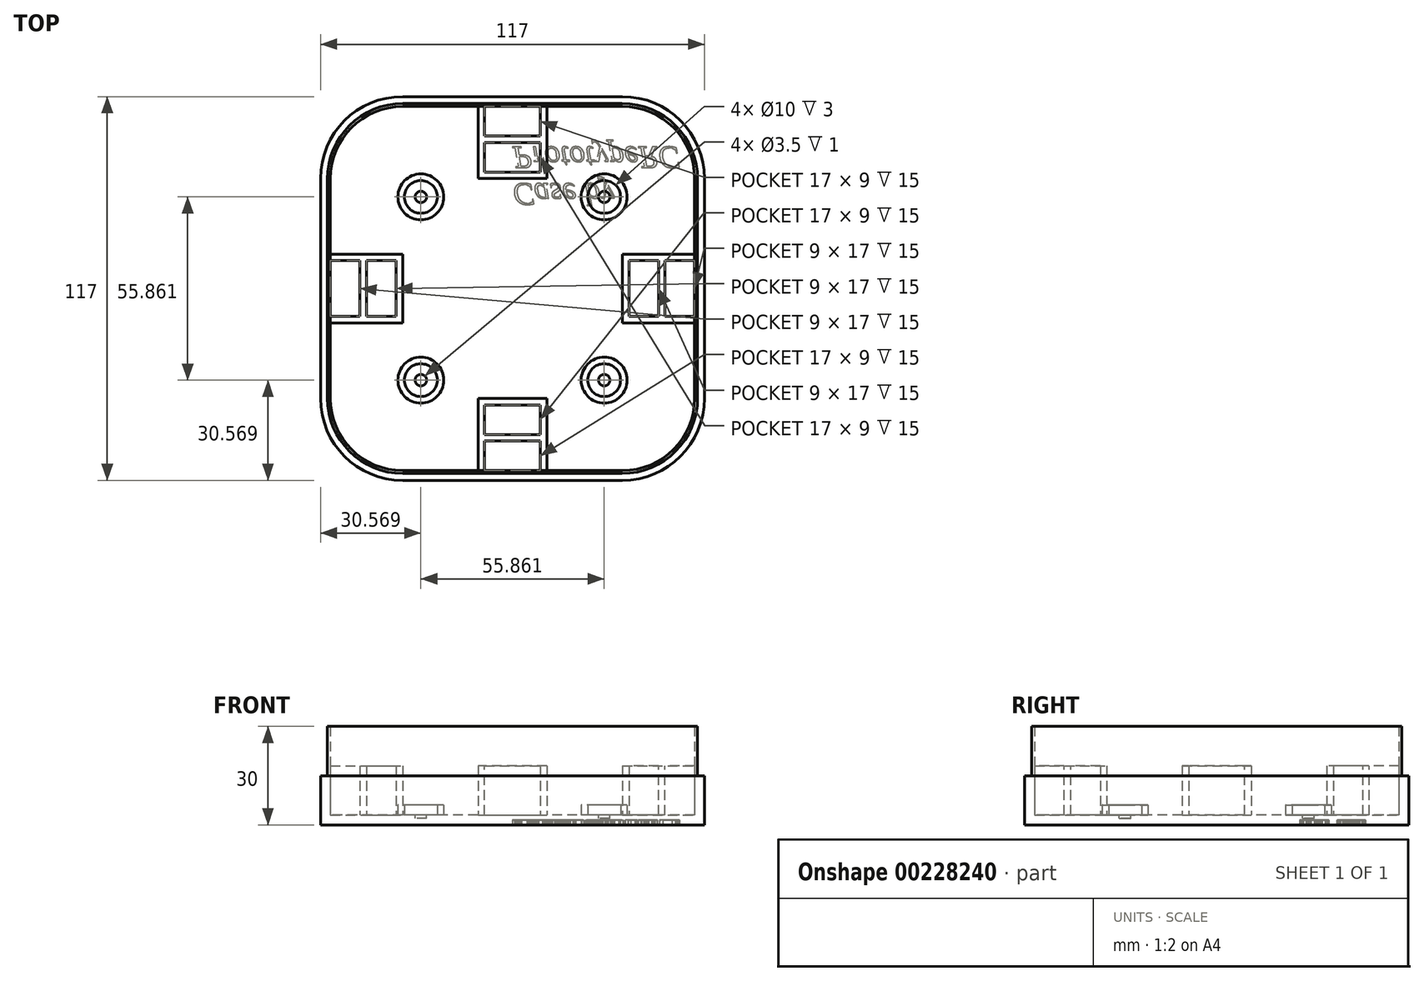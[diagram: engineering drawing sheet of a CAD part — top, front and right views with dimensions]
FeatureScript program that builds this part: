
annotation { "Feature Type Name" : "Feature", "Feature Type Description" : "" }
export const myFeature = defineFeature(function(context is Context, id is Id, definition is map)
    precondition{}
    {
        {
            var Q0;
            Q0=qCreatedBy(makeId("Top.planeOp"),FACE);
            var sketch = newSketch(context, id + "F0", { "sketchPlane" : qUnion([Q0])});
            skLineSegment(sketch, "E0.bottom", {"start": v(33.5, 58.5) * mm, "end": v(-33.5, 58.5) * mm});
            skLineSegment(sketch, "E0.top", {"start": v(33.5, -58.5) * mm, "end": v(-33.5, -58.5) * mm});
            skLineSegment(sketch, "E0.left", {"start": v(58.5, 33.5) * mm, "end": v(58.5, -33.5) * mm});
            skLineSegment(sketch, "E0.right", {"start": v(-58.5, 33.5) * mm, "end": v(-58.5, -33.5) * mm});
            skPoint(sketch, "E0.middle", {"position": v(0, 0) * mm});
            skPoint(sketch, "E1.visualSharp", {"position": v(-58.5, -58.5) * mm});
            skArc(sketch, "E1.filletArc", {"start": v(-58.5, -33.5) * mm, "mid": v(-51.18, -51.18) * mm, "end": v(-33.5, -58.5) * mm});
            skPoint(sketch, "E2.visualSharp", {"position": v(58.5, -58.5) * mm});
            skArc(sketch, "E2.filletArc", {"start": v(33.5, -58.5) * mm, "mid": v(51.18, -51.18) * mm, "end": v(58.5, -33.5) * mm});
            skPoint(sketch, "E3.visualSharp", {"position": v(58.5, 58.5) * mm});
            skArc(sketch, "E3.filletArc", {"start": v(58.5, 33.5) * mm, "mid": v(51.18, 51.18) * mm, "end": v(33.5, 58.5) * mm});
            skPoint(sketch, "E4.visualSharp", {"position": v(-58.5, 58.5) * mm});
            skArc(sketch, "E4.filletArc", {"start": v(-33.5, 58.5) * mm, "mid": v(-51.18, 51.18) * mm, "end": v(-58.5, 33.5) * mm});
            skSolve(sketch);
        }
        {
            var Q0;
            Q0 = qSketchRegion(id + "F0", true);
            extrude(context, id + "F1", {"entities" : qUnion([Q0]), "depth" : 30 * mm});
        }
        {
            var Q0;
            Q0=makeQuery(id+"F1.opExtrude","CAP_FACE",FACE,{"disambiguationData":[OSD([sQuery(id+"F0.wireOp",EDGE,"E0.bottom"),sQuery(id+"F0.wireOp",EDGE,"E0.top"),sQuery(id+"F0.wireOp",EDGE,"E0.left"),sQuery(id+"F0.wireOp",EDGE,"E0.right")])],"isStart":false});
            shell(context, id + "F2", {"entities" : qUnion([Q0]), "thickness" : 3 * mm});
        }
        {
            var Q0;
            Q0=makeQuery(id+"F1.opExtrude","CAP_FACE",FACE,{"disambiguationData":[OSD([sQuery(id+"F0.wireOp",EDGE,"E0.bottom"),sQuery(id+"F0.wireOp",EDGE,"E0.top"),sQuery(id+"F0.wireOp",EDGE,"E0.left"),sQuery(id+"F0.wireOp",EDGE,"E0.right")])],"isStart":false});
            var sketch = newSketch(context, id + "F3", { "sketchPlane" : qUnion([Q0])});
            skPoint(sketch, "E5.middle", {"position": v(0, 0) * mm});
            skLineSegment(sketch, "E6.bottom", {"start": v(33.4, 56.4) * mm, "end": v(-33.4, 56.4) * mm});
            skLineSegment(sketch, "E6.top", {"start": v(33.4, -56.4) * mm, "end": v(-33.4, -56.4) * mm});
            skLineSegment(sketch, "E6.left", {"start": v(56.4, 33.4) * mm, "end": v(56.4, -33.4) * mm});
            skLineSegment(sketch, "E6.right", {"start": v(-56.4, 33.4) * mm, "end": v(-56.4, -33.4) * mm});
            skPoint(sketch, "E7.visualSharp", {"position": v(56.4, 56.4) * mm});
            skArc(sketch, "E7.filletArc", {"start": v(56.4, 33.4) * mm, "mid": v(49.66, 49.66) * mm, "end": v(33.4, 56.4) * mm});
            skPoint(sketch, "E8.visualSharp", {"position": v(56.4, -56.4) * mm});
            skArc(sketch, "E8.filletArc", {"start": v(33.4, -56.4) * mm, "mid": v(49.66, -49.66) * mm, "end": v(56.4, -33.4) * mm});
            skPoint(sketch, "E9.visualSharp", {"position": v(-56.4, -56.4) * mm});
            skArc(sketch, "E9.filletArc", {"start": v(-56.4, -33.4) * mm, "mid": v(-49.66, -49.66) * mm, "end": v(-33.4, -56.4) * mm});
            skPoint(sketch, "E10.visualSharp", {"position": v(-56.4, 56.4) * mm});
            skArc(sketch, "E10.filletArc", {"start": v(-33.4, 56.4) * mm, "mid": v(-49.66, 49.66) * mm, "end": v(-56.4, 33.4) * mm});
            skLineSegment(sketch, "E11.bottom", {"start": v(33.5, 58.5) * mm, "end": v(-33.5, 58.5) * mm});
            skLineSegment(sketch, "E11.top", {"start": v(33.5, -58.5) * mm, "end": v(-33.5, -58.5) * mm});
            skLineSegment(sketch, "E11.left", {"start": v(58.5, 33.5) * mm, "end": v(58.5, -33.5) * mm});
            skLineSegment(sketch, "E11.right", {"start": v(-58.5, 33.5) * mm, "end": v(-58.5, -33.5) * mm});
            skPoint(sketch, "E12.visualSharp", {"position": v(-58.5, 58.5) * mm});
            skArc(sketch, "E12.filletArc", {"start": v(-33.5, 58.5) * mm, "mid": v(-51.18, 51.18) * mm, "end": v(-58.5, 33.5) * mm});
            skPoint(sketch, "E13.visualSharp", {"position": v(58.5, 58.5) * mm});
            skArc(sketch, "E13.filletArc", {"start": v(58.5, 33.5) * mm, "mid": v(51.18, 51.18) * mm, "end": v(33.5, 58.5) * mm});
            skPoint(sketch, "E14.visualSharp", {"position": v(58.5, -58.5) * mm});
            skArc(sketch, "E14.filletArc", {"start": v(33.5, -58.5) * mm, "mid": v(51.18, -51.18) * mm, "end": v(58.5, -33.5) * mm});
            skPoint(sketch, "E15.visualSharp", {"position": v(-58.5, -58.5) * mm});
            skArc(sketch, "E15.filletArc", {"start": v(-58.5, -33.5) * mm, "mid": v(-51.18, -51.18) * mm, "end": v(-33.5, -58.5) * mm});
            skSolve(sketch);
        }
        {
            var Q0;
            Q0 = qSketchRegion(id + "F3", true);
            extrude(context, id + "F4", {"entities" : qUnion([Q0]), "operationType" : NewBodyOperationType.REMOVE, "oppositeDirection" : true, "depth" : 15 * mm});
        }
        {
            var Q0;
            Q0=makeQuery(id+"F2.opShell","OFFSET_FACE",FACE,{"disambiguationData":[OSD([sQuery(id+"F0.wireOp",EDGE,"E0.bottom"),sQuery(id+"F0.wireOp",EDGE,"E0.top"),sQuery(id+"F0.wireOp",EDGE,"E0.left"),sQuery(id+"F0.wireOp",EDGE,"E0.right")])]});
            var sketch = newSketch(context, id + "F5", { "sketchPlane" : qUnion([Q0])});
            skLineSegment(sketch, "E16", {"start": v(-27.93, -27.93) * mm, "end": v(27.93, 27.93) * mm, "construction": true});
            skLineSegment(sketch, "E17", {"start": v(-27.93, 27.93) * mm, "end": v(27.93, -27.93) * mm, "construction": true});
            skCircle(sketch, "E18", {"center": v(27.93, 27.93) * mm, "radius": 1.75 * mm});
            skCircle(sketch, "E19", {"center": v(-27.93, 27.93) * mm, "radius": 1.75 * mm});
            skCircle(sketch, "E20", {"center": v(27.93, -27.93) * mm, "radius": 1.75 * mm});
            skCircle(sketch, "E21", {"center": v(-27.93, -27.93) * mm, "radius": 1.75 * mm});
            skSolve(sketch);
        }
        {
            var Q0;
            Q0 = qSketchRegion(id + "F5", true);
            extrude(context, id + "F6", {"entities" : qUnion([Q0]), "operationType" : NewBodyOperationType.REMOVE, "oppositeDirection" : true, "depth" : 1 * mm});
        }
        {
            var Q0;
            Q0=makeQuery(id+"F2.opShell","OFFSET_FACE",FACE,{"disambiguationData":[OSD([sQuery(id+"F0.wireOp",EDGE,"E0.bottom"),sQuery(id+"F0.wireOp",EDGE,"E0.top"),sQuery(id+"F0.wireOp",EDGE,"E0.left"),sQuery(id+"F0.wireOp",EDGE,"E0.right")])]});
            var sketch = newSketch(context, id + "F7", { "sketchPlane" : qUnion([Q0])});
            skCircle(sketch, "E22", {"center": v(-27.93, 27.93) * mm, "radius": 5 * mm});
            skCircle(sketch, "E23", {"center": v(27.93, 27.93) * mm, "radius": 5 * mm});
            skCircle(sketch, "E24", {"center": v(27.93, -27.93) * mm, "radius": 5 * mm});
            skCircle(sketch, "E25", {"center": v(-27.93, -27.93) * mm, "radius": 5 * mm});
            skCircle(sketch, "E26", {"center": v(-27.93, 27.93) * mm, "radius": 7 * mm});
            skCircle(sketch, "E27", {"center": v(27.93, 27.93) * mm, "radius": 7 * mm});
            skCircle(sketch, "E28", {"center": v(27.93, -27.93) * mm, "radius": 7 * mm});
            skCircle(sketch, "E29", {"center": v(-27.93, -27.93) * mm, "radius": 7 * mm});
            skSolve(sketch);
        }
        {
            var Q0;
            Q0 = qSketchRegion(id + "F7", true);
            extrude(context, id + "F8", {"entities" : qUnion([Q0]), "operationType" : NewBodyOperationType.ADD, "depth" : 3 * mm});
        }
        {
            var Q0;
            {var subQ0=sQuery(id+"F0.wireOp",EDGE,"E0.right");var subQ1=sQuery(id+"F0.wireOp",EDGE,"E0.left");var subQ2=sQuery(id+"F0.wireOp",EDGE,"E0.top");var subQ3=sQuery(id+"F0.wireOp",EDGE,"E0.bottom");Q0=makeQuery(id+"F8.boolean.opBoolean","SPLIT",FACE,{"disambiguationData":[TD([makeQuery(id+"F2.opShell","OFFSET_FACE",FACE,{"disambiguationData":[OSD([subQ3])]})])],"derivedFrom":makeQuery(id+"F2.opShell","OFFSET_FACE",FACE,{"disambiguationData":[OSD([subQ3,subQ2,subQ1,subQ0])]})});}
            var sketch = newSketch(context, id + "F9", { "sketchPlane" : qUnion([Q0])});
            skLineSegment(sketch, "E30", {"start": v(-10.5, 55.5) * mm, "end": v(-8.5, 55.5) * mm});
            skLineSegment(sketch, "E31", {"start": v(-8.5, 55.5) * mm, "end": v(-8.5, 35.5) * mm});
            skLineSegment(sketch, "E32", {"start": v(-8.5, 35.5) * mm, "end": v(8.5, 35.5) * mm});
            skLineSegment(sketch, "E33", {"start": v(8.5, 35.5) * mm, "end": v(8.5, 55.5) * mm});
            skLineSegment(sketch, "E34", {"start": v(8.5, 55.5) * mm, "end": v(10.5, 55.5) * mm});
            skLineSegment(sketch, "E35", {"start": v(10.5, 55.5) * mm, "end": v(10.5, 33.5) * mm});
            skLineSegment(sketch, "E36", {"start": v(10.5, 33.5) * mm, "end": v(-10.5, 33.5) * mm});
            skLineSegment(sketch, "E37", {"start": v(-10.5, 55.5) * mm, "end": v(-10.5, 33.5) * mm});
            skLineSegment(sketch, "E38", {"start": v(55.5, 10.5) * mm, "end": v(55.5, 8.5) * mm});
            skLineSegment(sketch, "E39", {"start": v(55.5, 8.5) * mm, "end": v(35.5, 8.5) * mm});
            skLineSegment(sketch, "E40", {"start": v(35.5, 8.5) * mm, "end": v(35.5, -8.5) * mm});
            skLineSegment(sketch, "E41", {"start": v(35.5, -8.5) * mm, "end": v(55.5, -8.5) * mm});
            skLineSegment(sketch, "E42", {"start": v(55.5, -8.5) * mm, "end": v(55.5, -10.5) * mm});
            skLineSegment(sketch, "E43", {"start": v(55.5, -10.5) * mm, "end": v(33.5, -10.5) * mm});
            skLineSegment(sketch, "E44", {"start": v(33.5, -10.5) * mm, "end": v(33.5, 10.5) * mm});
            skLineSegment(sketch, "E45", {"start": v(33.5, 10.5) * mm, "end": v(55.5, 10.5) * mm});
            skLineSegment(sketch, "E46", {"start": v(-8.5, -55.5) * mm, "end": v(-10.5, -55.5) * mm});
            skLineSegment(sketch, "E47", {"start": v(-10.5, -55.5) * mm, "end": v(-10.5, -33.5) * mm});
            skLineSegment(sketch, "E48", {"start": v(-10.5, -33.5) * mm, "end": v(10.5, -33.5) * mm});
            skLineSegment(sketch, "E49", {"start": v(10.5, -33.5) * mm, "end": v(10.5, -55.5) * mm});
            skLineSegment(sketch, "E50", {"start": v(10.5, -55.5) * mm, "end": v(8.5, -55.5) * mm});
            skLineSegment(sketch, "E51", {"start": v(8.5, -55.5) * mm, "end": v(8.5, -35.5) * mm});
            skLineSegment(sketch, "E52", {"start": v(8.5, -35.5) * mm, "end": v(-8.5, -35.5) * mm});
            skLineSegment(sketch, "E53", {"start": v(-8.5, -35.5) * mm, "end": v(-8.5, -55.5) * mm});
            skLineSegment(sketch, "E54", {"start": v(-55.5, 10.5) * mm, "end": v(-55.5, 8.5) * mm});
            skLineSegment(sketch, "E55", {"start": v(-55.5, 8.5) * mm, "end": v(-35.5, 8.5) * mm});
            skLineSegment(sketch, "E56", {"start": v(-35.5, 8.5) * mm, "end": v(-35.5, -8.5) * mm});
            skLineSegment(sketch, "E57", {"start": v(-35.5, -8.5) * mm, "end": v(-55.5, -8.5) * mm});
            skLineSegment(sketch, "E58", {"start": v(-55.5, -8.5) * mm, "end": v(-55.5, -10.5) * mm});
            skLineSegment(sketch, "E59", {"start": v(-55.5, -10.5) * mm, "end": v(-33.5, -10.5) * mm});
            skLineSegment(sketch, "E60", {"start": v(-33.5, -10.5) * mm, "end": v(-33.5, 10.5) * mm});
            skLineSegment(sketch, "E61", {"start": v(-33.5, 10.5) * mm, "end": v(-55.5, 10.5) * mm});
            skSolve(sketch);
        }
        {
            var Q0;
            Q0 = qSketchRegion(id + "F9", true);
            extrude(context, id + "F10", {"entities" : qUnion([Q0]), "operationType" : NewBodyOperationType.ADD, "depth" : 15 * mm});
        }
        {
            var Q0;
            {var subQ0=sQuery(id+"F0.wireOp",EDGE,"E0.right");var subQ2=sQuery(id+"F0.wireOp",EDGE,"E4.filletArc");var subQ3=sQuery(id+"F0.wireOp",EDGE,"E3.filletArc");var subQ4=sQuery(id+"F0.wireOp",EDGE,"E2.filletArc");var subQ5=sQuery(id+"F0.wireOp",EDGE,"E1.filletArc");var subQ6=sQuery(id+"F0.wireOp",EDGE,"E0.bottom");var subQ7=sQuery(id+"F0.wireOp",EDGE,"E0.top");var subQ8=sQuery(id+"F0.wireOp",EDGE,"E0.left");Q0=makeQuery(id+"F10.boolean.opBoolean","SPLIT",FACE,{"disambiguationData":[TD([makeQuery(id+"F10.opExtrude","SWEPT_FACE",FACE,{"disambiguationData":[OSD([sQuery(id+"F9.wireOp",EDGE,"E55")])]})])],"derivedFrom":makeQuery(id+"F8.boolean.opBoolean","SPLIT",FACE,{"disambiguationData":[TD([makeQuery(id+"F2.opShell","OFFSET_FACE",FACE,{"disambiguationData":[OSD([subQ6])]})])],"derivedFrom":makeQuery(id+"F2.opShell","OFFSET_FACE",FACE,{"disambiguationData":[OSD([subQ6,subQ7,subQ8,subQ0,subQ5,subQ4,subQ3,subQ2])]})})});}
            var sketch = newSketch(context, id + "F11", { "sketchPlane" : qUnion([Q0])});
            skLineSegment(sketch, "E62.bottom", {"start": v(-46.5, 10.5) * mm, "end": v(-44.5, 10.5) * mm});
            skLineSegment(sketch, "E62.top", {"start": v(-46.5, -10.5) * mm, "end": v(-44.5, -10.5) * mm});
            skLineSegment(sketch, "E62.left", {"start": v(-46.5, 10.5) * mm, "end": v(-46.5, -10.5) * mm});
            skLineSegment(sketch, "E62.right", {"start": v(-44.5, 10.5) * mm, "end": v(-44.5, -10.5) * mm});
            skLineSegment(sketch, "E63.bottom", {"start": v(44.5, 10.5) * mm, "end": v(46.5, 10.5) * mm});
            skLineSegment(sketch, "E63.top", {"start": v(44.5, -10.5) * mm, "end": v(46.5, -10.5) * mm});
            skLineSegment(sketch, "E63.left", {"start": v(44.5, 10.5) * mm, "end": v(44.5, -10.5) * mm});
            skLineSegment(sketch, "E63.right", {"start": v(46.5, 10.5) * mm, "end": v(46.5, -10.5) * mm});
            skLineSegment(sketch, "E64.bottom", {"start": v(-10.5, -44.5) * mm, "end": v(10.5, -44.5) * mm});
            skLineSegment(sketch, "E64.top", {"start": v(-10.5, -46.5) * mm, "end": v(10.5, -46.5) * mm});
            skLineSegment(sketch, "E64.left", {"start": v(-10.5, -44.5) * mm, "end": v(-10.5, -46.5) * mm});
            skLineSegment(sketch, "E64.right", {"start": v(10.5, -44.5) * mm, "end": v(10.5, -46.5) * mm});
            skLineSegment(sketch, "E65.bottom", {"start": v(-10.5, 46.5) * mm, "end": v(10.5, 46.5) * mm});
            skLineSegment(sketch, "E65.top", {"start": v(-10.5, 44.5) * mm, "end": v(10.5, 44.5) * mm});
            skLineSegment(sketch, "E65.left", {"start": v(-10.5, 46.5) * mm, "end": v(-10.5, 44.5) * mm});
            skLineSegment(sketch, "E65.right", {"start": v(10.5, 46.5) * mm, "end": v(10.5, 44.5) * mm});
            skSolve(sketch);
        }
        {
            var Q0;
            Q0 = qSketchRegion(id + "F11", true);
            extrude(context, id + "F12", {"entities" : qUnion([Q0]), "operationType" : NewBodyOperationType.ADD, "depth" : 15 * mm});
        }
        {
            var Q0;
            Q0=makeQuery(id+"F1.opExtrude","CAP_FACE",FACE,{"disambiguationData":[OSD([sQuery(id+"F0.wireOp",EDGE,"E0.bottom"),sQuery(id+"F0.wireOp",EDGE,"E0.top"),sQuery(id+"F0.wireOp",EDGE,"E0.left"),sQuery(id+"F0.wireOp",EDGE,"E0.right"),sQuery(id+"F0.wireOp",EDGE,"E1.filletArc"),sQuery(id+"F0.wireOp",EDGE,"E2.filletArc"),sQuery(id+"F0.wireOp",EDGE,"E3.filletArc"),sQuery(id+"F0.wireOp",EDGE,"E4.filletArc")])],"isStart":true});
            var sketch = newSketch(context, id + "F13", { "sketchPlane" : qUnion([Q0])});
            skText(sketch, "E66", { "text": "Case by\nPrototypeRC", "fontName": "Tinos-Italic.ttf"});
            const initialGuessF13  = {"E66": [0, -0.032, 1, 0, 0.007]};
            skSetInitialGuess(sketch, initialGuessF13);
            skSolve(sketch);
        }
        {
            var Q0;
            Q0 = qSketchRegion(id + "F13", true);
            extrude(context, id + "F14", {"entities" : qUnion([Q0]), "operationType" : NewBodyOperationType.REMOVE, "oppositeDirection" : true, "depth" : 1.5 * mm});
        }
    });
